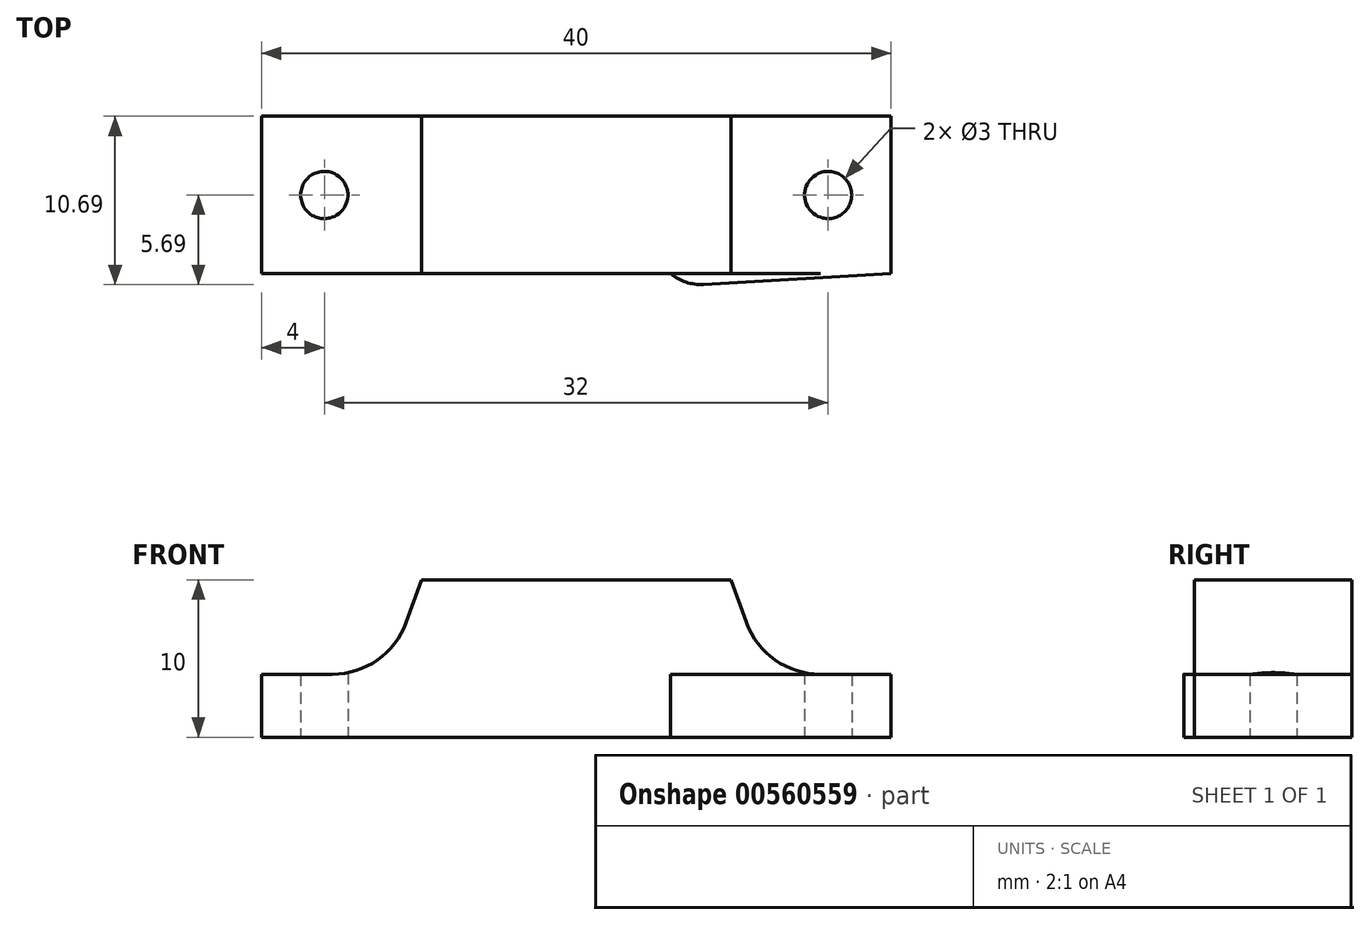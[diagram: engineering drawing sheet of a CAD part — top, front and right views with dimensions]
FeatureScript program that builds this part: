
annotation { "Feature Type Name" : "Feature", "Feature Type Description" : "" }
export const myFeature = defineFeature(function(context is Context, id is Id, definition is map)
    precondition{}
    {
        {
            var Q0;
            Q0=qCreatedBy(makeId("Front.planeOp"),FACE);
            var sketch = newSketch(context, id + "F0", { "sketchPlane" : qUnion([Q0])});
            skLineSegment(sketch, "E0.bottom", {"start": v(0, 0) * mm, "end": v(40, 0) * mm});
            skLineSegment(sketch, "E1", {"start": v(0, 4) * mm, "end": v(8, 4) * mm});
            skLineSegment(sketch, "E2", {"start": v(8, 4) * mm, "end": v(10.18, 10) * mm});
            skLineSegment(sketch, "E3", {"start": v(10.18, 10) * mm, "end": v(29.82, 10) * mm});
            skLineSegment(sketch, "E4", {"start": v(29.82, 10) * mm, "end": v(32, 4) * mm});
            skLineSegment(sketch, "E5", {"start": v(32, 4) * mm, "end": v(40, 4) * mm});
            skLineSegment(sketch, "E6", {"start": v(0, 4) * mm, "end": v(0, 0) * mm});
            skLineSegment(sketch, "E7", {"start": v(40, 4) * mm, "end": v(40, 0) * mm});
            skSolve(sketch);
        }
        {
            var Q0;
            Q0 = qSketchRegion(id + "F0", true);
            var Q1;
            Q1 = qConstructionFilter(qBodyType(qCreatedBy(id + "F0" ,EDGE), BodyType.WIRE), ConstructionObject.NO);
            extrude(context, id + "F1", {"entities" : qUnion([Q0]), "surfaceEntities" : qUnion([Q1]), "endBound" : BoundingType.SYMMETRIC, "depth" : 10 * mm, "offsetDistance" : 25 * mm});
        }
        {
            var Q0;
            Q0=makeQuery(id+"F1.opExtrude","SWEPT_EDGE",EDGE,{"disambiguationData":[OSD([sQuery(id+"F0.wireOp",EDGE,"E4"),sQuery(id+"F0.wireOp",EDGE,"E5")])]});
            var Q1;
            Q1=makeQuery(id+"F1.opExtrude","SWEPT_EDGE",EDGE,{"disambiguationData":[OSD([sQuery(id+"F0.wireOp",EDGE,"E1"),sQuery(id+"F0.wireOp",EDGE,"E2")])]});
            fillet(context, id + "F2", {"entities" : qUnion([Q0, Q1]), "radius" : 5 * mm, "tangentPropagation" : true, "allowEdgeOverflow" : false});
        }
        {
            var Q0;
            Q0=qCreatedBy(makeId("Top.planeOp"),FACE);
            var sketch = newSketch(context, id + "F3", { "sketchPlane" : qUnion([Q0])});
            skCircle(sketch, "E8", {"center": v(4, 0) * mm, "radius": 1.5 * mm});
            skCircle(sketch, "E9", {"center": v(36, 0) * mm, "radius": 1.5 * mm});
            skSolve(sketch);
        }
        {
            var Q0;
            Q0 = qSketchRegion(id + "F3", true);
            extrude(context, id + "F4", {"entities" : qUnion([Q0]), "operationType" : NewBodyOperationType.REMOVE, "depth" : 25 * mm, "offsetDistance" : 25 * mm});
        }
        {
            var Q0;
            Q0=qCreatedBy(makeId("Top.planeOp"),FACE);
            var sketch = newSketch(context, id + "F5", { "sketchPlane" : qUnion([Q0])});
            skLineSegment(sketch, "E10", {"start": v(40, -5) * mm, "end": v(26, -5.8) * mm});
            skLineSegment(sketch, "E11", {"start": v(26, -5.8) * mm, "end": v(26, -5) * mm});
            skLineSegment(sketch, "E12", {"start": v(26, -5) * mm, "end": v(40, -5) * mm});
            skSolve(sketch);
        }
        {
            var Q0;
            Q0 = qSketchRegion(id + "F5", true);
            extrude(context, id + "F6", {"entities" : qUnion([Q0]), "operationType" : NewBodyOperationType.ADD, "depth" : 4 * mm, "offsetDistance" : 25 * mm});
        }
        {
            var Q0;
            Q0=makeQuery(id+"F6.opExtrude","SWEPT_EDGE",EDGE,{"disambiguationData":[OSD([sQuery(id+"F5.wireOp",EDGE,"E10"),sQuery(id+"F5.wireOp",EDGE,"E11")])]});
            fillet(context, id + "F7", {"entities" : qUnion([Q0]), "radius" : 3 * mm, "tangentPropagation" : true, "allowEdgeOverflow" : false});
        }
    });
